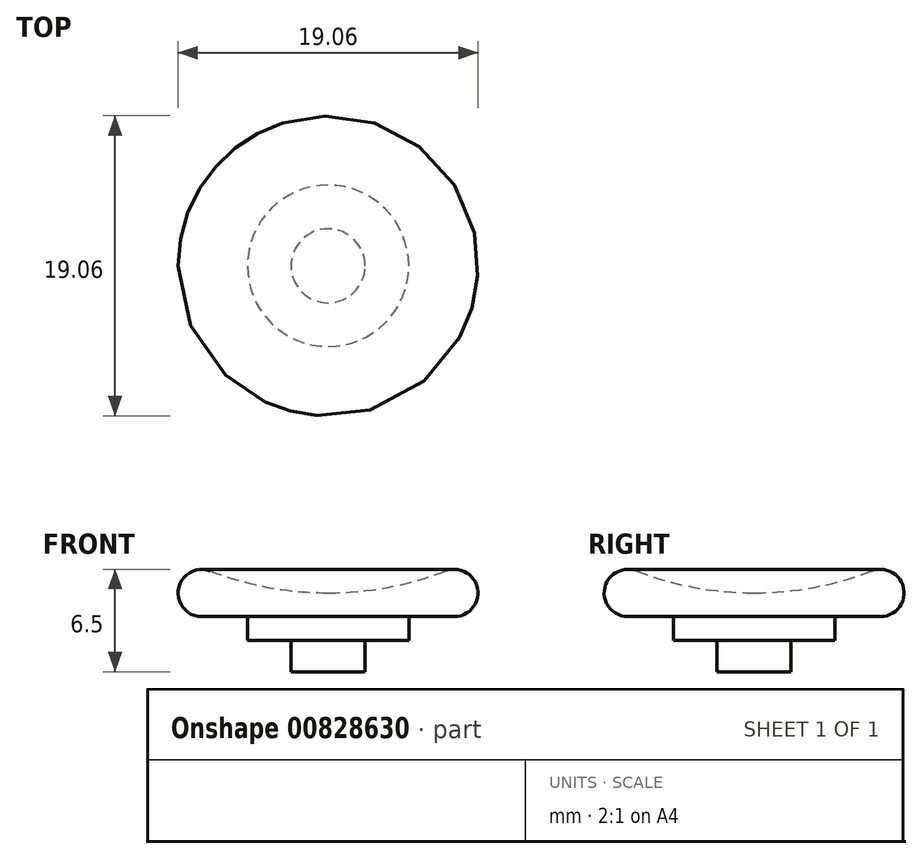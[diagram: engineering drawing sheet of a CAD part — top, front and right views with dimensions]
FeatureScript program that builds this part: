
annotation { "Feature Type Name" : "Feature", "Feature Type Description" : "" }
export const myFeature = defineFeature(function(context is Context, id is Id, definition is map)
    precondition{}
    {
        {
            var Q0;
            Q0=qCreatedBy(makeId("Front.planeOp"),FACE);
            var sketch = newSketch(context, id + "F0", { "sketchPlane" : qUnion([Q0])});
            skArc(sketch, "E0", {"start": v(-7.49, 2.9) * mm, "mid": v(-9.5, 1.77) * mm, "end": v(-8.03, 0) * mm});
            skArc(sketch, "E1", {"start": v(-7.49, 2.9) * mm, "mid": v(-3.8, 1.86) * mm, "end": v(0, 1.51) * mm});
            skLineSegment(sketch, "E2", {"start": v(0, 0) * mm, "end": v(0, 1.51) * mm});
            skLineSegment(sketch, "E3", {"start": v(-8.03, 0) * mm, "end": v(0, 0) * mm});
            skPoint(sketch, "E4.orphan", {"position": v(-28.3, 0) * mm});
            skPoint(sketch, "E5.startSnap0", {"position": v(-9.5, 1.77) * mm});
            skSolve(sketch);
        }
        {
            var Q0;
            Q0=qSketchRegion(id+"F0",true);
            var Q1;
            Q1=makeQuery(id+"F0.imprint","IMPRINT",FACE,{"disambiguationData":[TD([[makeQuery(id+"F0.imprint","IMPRINT",EDGE,{"derivedFrom":sQuery(id+"F0.wireOp",EDGE,"E0")}),1.0]])]});
            var Q2;
            Q2=sQuery(id+"F0.wireOp",EDGE,"E2");
            revolve(context, id + "F1", {"surfaceOperationType" : NewSurfaceOperationType.NEW, "entities" : qUnion([Q0, Q1]), "axis" : qUnion([Q2]), "revolveType" : RevolveType.FULL});
        }
        {
            var Q0;
            Q0=qCreatedBy(makeId("Top.planeOp"),FACE);
            var sketch = newSketch(context, id + "F2", { "sketchPlane" : qUnion([Q0])});
            skCircle(sketch, "E6", {"center": v(0, 0) * mm, "radius": 5.12 * mm});
            skSolve(sketch);
        }
        {
            var Q0;
            Q0=qSketchRegion(id+"F2",true);
            extrude(context, id + "F3", {"entities" : qUnion([Q0]), "operationType" : NewBodyOperationType.ADD, "oppositeDirection" : true, "depth" : 1.5 * mm, "offsetDistance" : 25 * mm});
        }
        {
            var Q0;
            Q0=qCreatedBy(makeId("Top.planeOp"),FACE);
            var sketch = newSketch(context, id + "F4", { "sketchPlane" : qUnion([Q0])});
            skCircle(sketch, "E7", {"center": v(0, 0) * mm, "radius": 2.35 * mm});
            skSolve(sketch);
        }
        {
            var Q0;
            Q0=qSketchRegion(id+"F4",true);
            extrude(context, id + "F5", {"entities" : qUnion([Q0]), "operationType" : NewBodyOperationType.ADD, "oppositeDirection" : true, "depth" : 3.5 * mm, "offsetDistance" : 25 * mm});
        }
    });
